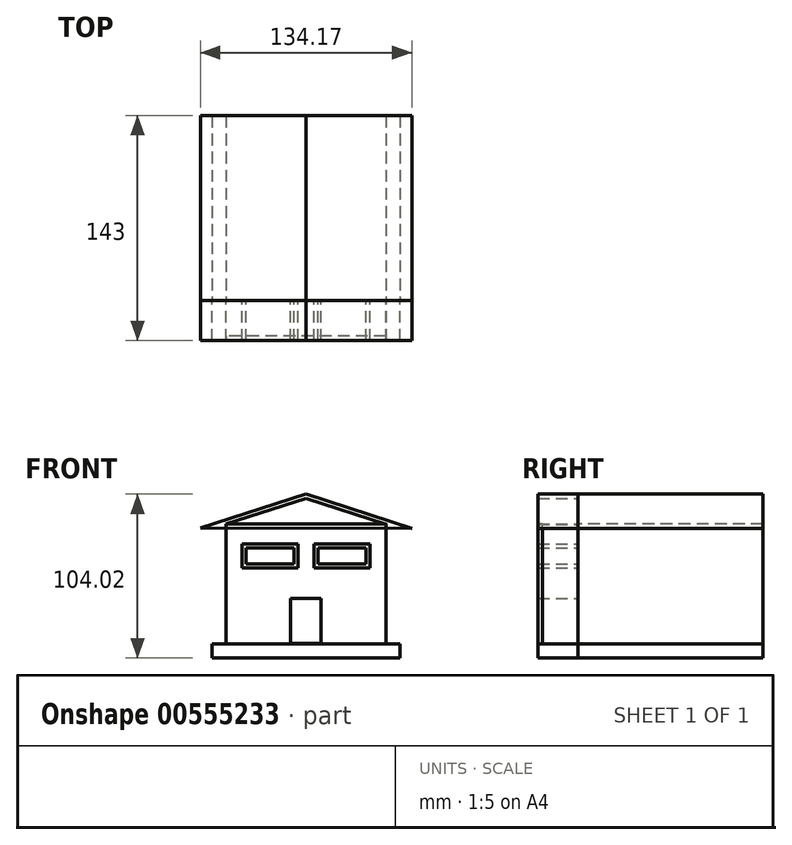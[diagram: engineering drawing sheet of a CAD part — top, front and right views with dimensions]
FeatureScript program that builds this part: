
annotation { "Feature Type Name" : "Feature", "Feature Type Description" : "" }
export const myFeature = defineFeature(function(context is Context, id is Id, definition is map)
    precondition{}
    {
        {
            var Q0;
            Q0=qCreatedBy(makeId("Front.planeOp"),FACE);
            var sketch = newSketch(context, id + "F0", { "sketchPlane" : qUnion([Q0])});
            skLineSegment(sketch, "E0.bottom", {"start": v(50.8, -38.1) * mm, "end": v(-50.8, -38.1) * mm});
            skLineSegment(sketch, "E0.top", {"start": v(50.8, 38.1) * mm, "end": v(-50.8, 38.1) * mm});
            skLineSegment(sketch, "E0.left", {"start": v(50.8, -38.1) * mm, "end": v(50.8, 38.1) * mm});
            skLineSegment(sketch, "E0.right", {"start": v(-50.8, -38.1) * mm, "end": v(-50.8, 38.1) * mm});
            skPoint(sketch, "E0.middle", {"position": v(0, 0) * mm});
            skSolve(sketch);
        }
        {
            var Q0;
            Q0=qCreatedBy(makeId("Front.planeOp"),FACE);
            var sketch = newSketch(context, id + "F1", { "sketchPlane" : qUnion([Q0])});
            skLineSegment(sketch, "E1.bottom", {"start": v(9.63, -37.6) * mm, "end": v(-9.63, -37.6) * mm});
            skLineSegment(sketch, "E1.top", {"start": v(9.63, -9.32) * mm, "end": v(-9.63, -9.32) * mm});
            skLineSegment(sketch, "E1.left", {"start": v(9.63, -37.6) * mm, "end": v(9.63, -9.32) * mm});
            skLineSegment(sketch, "E1.right", {"start": v(-9.63, -37.6) * mm, "end": v(-9.63, -9.32) * mm});
            skPoint(sketch, "E1.middle", {"position": v(0, -23.46) * mm});
            skSolve(sketch);
        }
        {
            var Q0;
            Q0=makeQuery(id+"F0.imprint","IMPRINT",FACE,{"disambiguationData":[TD([[makeQuery(id+"F0.imprint","IMPRINT",EDGE,{"derivedFrom":sQuery(id+"F0.wireOp",EDGE,"E0.bottom")}),-1.0]])]});
            var sketch = newSketch(context, id + "F2", { "sketchPlane" : qUnion([Q0])});
            skLineSegment(sketch, "E2.bottom", {"start": v(-41.8, -12.93) * mm, "end": v(-16.84, -12.93) * mm});
            skLineSegment(sketch, "E2.top", {"start": v(-41.8, -27.37) * mm, "end": v(-16.84, -27.37) * mm});
            skLineSegment(sketch, "E2.left", {"start": v(-41.8, -12.93) * mm, "end": v(-41.8, -27.37) * mm});
            skLineSegment(sketch, "E2.right", {"start": v(-16.84, -12.93) * mm, "end": v(-16.84, -27.37) * mm});
            skSolve(sketch);
        }
        {
            var Q0;
            Q0=makeQuery(id+"F0.imprint","IMPRINT",FACE,{"disambiguationData":[TD([[makeQuery(id+"F0.imprint","IMPRINT",EDGE,{"derivedFrom":sQuery(id+"F0.wireOp",EDGE,"E0.bottom")}),-1.0]])]});
            var sketch = newSketch(context, id + "F3", { "sketchPlane" : qUnion([Q0])});
            skLineSegment(sketch, "E3.0", {"start": v(-44.35, -10.4) * mm, "end": v(-14.3, -10.4) * mm});
            skLineSegment(sketch, "E3.1", {"start": v(-44.35, -10.4) * mm, "end": v(-44.35, -29.91) * mm});
            skLineSegment(sketch, "E3.2", {"start": v(-44.35, -29.91) * mm, "end": v(-14.3, -29.91) * mm});
            skLineSegment(sketch, "E3.3", {"start": v(-14.3, -10.4) * mm, "end": v(-14.3, -29.91) * mm});
            skSolve(sketch);
        }
        {
            var Q0;
            Q0=makeQuery(id+"F0.imprint","IMPRINT",FACE,{"disambiguationData":[TD([[makeQuery(id+"F0.imprint","IMPRINT",EDGE,{"derivedFrom":sQuery(id+"F0.wireOp",EDGE,"E0.bottom")}),-1.0]])]});
            var sketch = newSketch(context, id + "F4", { "sketchPlane" : qUnion([Q0])});
            skLineSegment(sketch, "E4.bottom", {"start": v(15.04, -13.54) * mm, "end": v(44.82, -13.54) * mm});
            skLineSegment(sketch, "E4.top", {"start": v(15.04, -28.88) * mm, "end": v(44.82, -28.88) * mm});
            skLineSegment(sketch, "E4.left", {"start": v(15.04, -13.54) * mm, "end": v(15.04, -28.88) * mm});
            skLineSegment(sketch, "E4.right", {"start": v(44.82, -13.54) * mm, "end": v(44.82, -28.88) * mm});
            skSolve(sketch);
        }
        {
            var Q0;
            Q0=makeQuery(id+"F0.imprint","IMPRINT",FACE,{"disambiguationData":[TD([[makeQuery(id+"F0.imprint","IMPRINT",EDGE,{"derivedFrom":sQuery(id+"F0.wireOp",EDGE,"E0.bottom")}),-1.0]])]});
            var sketch = newSketch(context, id + "F5", { "sketchPlane" : qUnion([Q0])});
            skLineSegment(sketch, "E5.0", {"start": v(12.5, -11) * mm, "end": v(47.36, -11) * mm});
            skLineSegment(sketch, "E5.1", {"start": v(12.5, -11) * mm, "end": v(12.5, -31.42) * mm});
            skLineSegment(sketch, "E5.2", {"start": v(12.5, -31.42) * mm, "end": v(47.36, -31.42) * mm});
            skLineSegment(sketch, "E5.3", {"start": v(47.36, -11) * mm, "end": v(47.36, -31.42) * mm});
            skSolve(sketch);
        }
        {
            var Q0;
            Q0=qCreatedBy(makeId("Front.planeOp"),FACE);
            var sketch = newSketch(context, id + "F6", { "sketchPlane" : qUnion([Q0])});
            skLineSegment(sketch, "E6.bottom", {"start": v(-38.1, 22.86) * mm, "end": v(-7.62, 22.86) * mm});
            skLineSegment(sketch, "E6.top", {"start": v(-38.1, 12.7) * mm, "end": v(-7.62, 12.7) * mm});
            skLineSegment(sketch, "E6.left", {"start": v(-38.1, 22.86) * mm, "end": v(-38.1, 12.7) * mm});
            skLineSegment(sketch, "E6.right", {"start": v(-7.62, 22.86) * mm, "end": v(-7.62, 12.7) * mm});
            skLineSegment(sketch, "E7.bottom", {"start": v(7.62, 22.86) * mm, "end": v(38.1, 22.86) * mm});
            skLineSegment(sketch, "E7.top", {"start": v(7.62, 12.7) * mm, "end": v(38.1, 12.7) * mm});
            skLineSegment(sketch, "E7.left", {"start": v(7.62, 22.86) * mm, "end": v(7.62, 12.7) * mm});
            skLineSegment(sketch, "E7.right", {"start": v(38.1, 22.86) * mm, "end": v(38.1, 12.7) * mm});
            skSolve(sketch);
        }
        {
            var Q0;
            Q0=qCreatedBy(makeId("Front.planeOp"),FACE);
            var sketch = newSketch(context, id + "F7", { "sketchPlane" : qUnion([Q0])});
            skLineSegment(sketch, "E8.0", {"start": v(-40.64, 25.4) * mm, "end": v(-5.08, 25.4) * mm});
            skLineSegment(sketch, "E8.1", {"start": v(-40.64, 25.4) * mm, "end": v(-40.64, 10.16) * mm});
            skLineSegment(sketch, "E8.2", {"start": v(-40.64, 10.16) * mm, "end": v(-5.08, 10.16) * mm});
            skLineSegment(sketch, "E8.3", {"start": v(-5.08, 25.4) * mm, "end": v(-5.08, 10.16) * mm});
            skLineSegment(sketch, "E9.0", {"start": v(40.64, 25.4) * mm, "end": v(40.64, 10.16) * mm});
            skLineSegment(sketch, "E9.1", {"start": v(5.08, 25.4) * mm, "end": v(40.64, 25.4) * mm});
            skLineSegment(sketch, "E9.2", {"start": v(5.08, 25.4) * mm, "end": v(5.08, 10.16) * mm});
            skLineSegment(sketch, "E9.3", {"start": v(5.08, 10.16) * mm, "end": v(40.64, 10.16) * mm});
            skSolve(sketch);
        }
        {
            var Q0;
            Q0=qCreatedBy(makeId("Front.planeOp"),FACE);
            var sketch = newSketch(context, id + "F8", { "sketchPlane" : qUnion([Q0])});
            skLineSegment(sketch, "E10", {"start": v(-50.8, 38.1) * mm, "end": v(0, 54.36) * mm});
            skLineSegment(sketch, "E11", {"start": v(0, 54.36) * mm, "end": v(51.1, 37.73) * mm});
            skLineSegment(sketch, "E12", {"start": v(51.1, 37.73) * mm, "end": v(-50.8, 38.1) * mm});
            skSolve(sketch);
        }
        {
            var Q0;
            Q0=qCreatedBy(makeId("Front.planeOp"),FACE);
            var sketch = newSketch(context, id + "F9", { "sketchPlane" : qUnion([Q0])});
            skLineSegment(sketch, "E13.0", {"start": v(-66.88, 35.62) * mm, "end": v(0, 57.03) * mm});
            skLineSegment(sketch, "E13.1", {"start": v(67.29, 35.13) * mm, "end": v(-66.88, 35.62) * mm});
            skLineSegment(sketch, "E13.2", {"start": v(0, 57.03) * mm, "end": v(67.29, 35.13) * mm});
            skSolve(sketch);
        }
        {
            var Q0;
            Q0=qCreatedBy(makeId("Front.planeOp"),FACE);
            var sketch = newSketch(context, id + "F10", { "sketchPlane" : qUnion([Q0])});
            skLineSegment(sketch, "E14.bottom", {"start": v(-59.7, -38.1) * mm, "end": v(59.7, -38.1) * mm});
            skLineSegment(sketch, "E14.top", {"start": v(-59.7, -46.99) * mm, "end": v(59.7, -46.99) * mm});
            skLineSegment(sketch, "E14.left", {"start": v(-59.7, -38.1) * mm, "end": v(-59.7, -46.99) * mm});
            skLineSegment(sketch, "E14.right", {"start": v(59.7, -38.1) * mm, "end": v(59.7, -46.99) * mm});
            skSolve(sketch);
        }
        {
            var Q0;
            Q0=makeQuery(id+"F8.imprint","IMPRINT",FACE,{"disambiguationData":[TD([[makeQuery(id+"F8.imprint","IMPRINT",EDGE,{"derivedFrom":sQuery(id+"F8.wireOp",EDGE,"E10")}),-1.0]])]});
            var Q1;
            Q1=makeQuery(id+"F6.imprint","IMPRINT",FACE,{"disambiguationData":[TD([[makeQuery(id+"F6.imprint","IMPRINT",EDGE,{"derivedFrom":sQuery(id+"F6.wireOp",EDGE,"E6.bottom")}),-1.0]])]});
            var Q2;
            Q2=makeQuery(id+"F2.imprint","IMPRINT",FACE,{"disambiguationData":[TD([[makeQuery(id+"F2.imprint","IMPRINT",EDGE,{"derivedFrom":sQuery(id+"F2.wireOp",EDGE,"E2.bottom")}),-1.0]])]});
            var Q3;
            Q3=makeQuery(id+"F2.imprint","IMPRINT",FACE,{"disambiguationData":[TD([[makeQuery(id+"F2.imprint","IMPRINT",EDGE,{"derivedFrom":sQuery(id+"F2.wireOp",EDGE,"E2.bottom")}),1.0]])]});
            var Q4;
            Q4=makeQuery(id+"F6.imprint","IMPRINT",FACE,{"disambiguationData":[TD([[makeQuery(id+"F6.imprint","IMPRINT",EDGE,{"derivedFrom":sQuery(id+"F6.wireOp",EDGE,"E7.bottom")}),-1.0]])]});
            var Q5;
            Q5=makeQuery(id+"F3.imprint","IMPRINT",FACE,{"disambiguationData":[TD([[makeQuery(id+"F3.imprint","IMPRINT",EDGE,{"derivedFrom":sQuery(id+"F3.wireOp",EDGE,"E3.0")}),-1.0]])]});
            var Q6;
            Q6=makeQuery(id+"F3.imprint","IMPRINT",FACE,{"disambiguationData":[TD([[makeQuery(id+"F3.imprint","IMPRINT",EDGE,{"derivedFrom":sQuery(id+"F3.wireOp",EDGE,"E3.0")}),1.0]])]});
            var Q7;
            Q7=makeQuery(id+"F0.imprint","IMPRINT",FACE,{"disambiguationData":[TD([[makeQuery(id+"F0.imprint","IMPRINT",EDGE,{"derivedFrom":sQuery(id+"F0.wireOp",EDGE,"E0.bottom")}),-1.0]])]});
            var Q8;
            Q8=makeQuery(id+"F4.imprint","IMPRINT",FACE,{"disambiguationData":[TD([[makeQuery(id+"F4.imprint","IMPRINT",EDGE,{"derivedFrom":sQuery(id+"F4.wireOp",EDGE,"E4.bottom")}),-1.0]])]});
            var Q9;
            Q9=makeQuery(id+"F4.imprint","IMPRINT",FACE,{"disambiguationData":[TD([[makeQuery(id+"F4.imprint","IMPRINT",EDGE,{"derivedFrom":sQuery(id+"F4.wireOp",EDGE,"E4.bottom")}),1.0]])]});
            var Q10;
            Q10=makeQuery(id+"F9.imprint","IMPRINT",FACE,{"disambiguationData":[TD([[makeQuery(id+"F9.imprint","IMPRINT",EDGE,{"derivedFrom":sQuery(id+"F9.wireOp",EDGE,"E13.0")}),-1.0]])]});
            var Q11;
            Q11=makeQuery(id+"F5.imprint","IMPRINT",FACE,{"disambiguationData":[TD([[makeQuery(id+"F5.imprint","IMPRINT",EDGE,{"derivedFrom":sQuery(id+"F5.wireOp",EDGE,"E5.0")}),-1.0]])]});
            var Q12;
            Q12=makeQuery(id+"F5.imprint","IMPRINT",FACE,{"disambiguationData":[TD([[makeQuery(id+"F5.imprint","IMPRINT",EDGE,{"derivedFrom":sQuery(id+"F5.wireOp",EDGE,"E5.0")}),1.0]])]});
            var Q13;
            Q13=makeQuery(id+"F1.imprint","IMPRINT",FACE,{"disambiguationData":[TD([[makeQuery(id+"F1.imprint","IMPRINT",EDGE,{"derivedFrom":sQuery(id+"F1.wireOp",EDGE,"E1.bottom")}),-1.0]])]});
            var Q14;
            Q14=makeQuery(id+"F7.imprint","IMPRINT",FACE,{"disambiguationData":[TD([[makeQuery(id+"F7.imprint","IMPRINT",EDGE,{"derivedFrom":sQuery(id+"F7.wireOp",EDGE,"E8.0")}),-1.0]])]});
            var Q15;
            Q15=makeQuery(id+"F7.imprint","IMPRINT",FACE,{"disambiguationData":[TD([[makeQuery(id+"F7.imprint","IMPRINT",EDGE,{"derivedFrom":sQuery(id+"F7.wireOp",EDGE,"E9.0")}),-1.0]])]});
            var Q16;
            Q16=makeQuery(id+"F10.imprint","IMPRINT",FACE,{"disambiguationData":[TD([[makeQuery(id+"F10.imprint","IMPRINT",EDGE,{"derivedFrom":sQuery(id+"F10.wireOp",EDGE,"E14.bottom")}),-1.0]])]});
            extrude(context, id + "F11", {"entities" : qUnion([Q0, Q1, Q2, Q3, Q4, Q5, Q6, Q7, Q8, Q9, Q10, Q11, Q12, Q13, Q14, Q15, Q16]), "depth" : 25.4 * mm, "offsetDistance" : 25.4 * mm});
        }
        {
            var Q0;
            Q0=makeQuery(id+"F11.opExtrude","CAP_FACE",FACE,{"disambiguationData":[OSD([sQuery(id+"F10.wireOp",EDGE,"E14.bottom"),sQuery(id+"F10.wireOp",EDGE,"E14.top"),sQuery(id+"F10.wireOp",EDGE,"E14.left"),sQuery(id+"F10.wireOp",EDGE,"E14.right")])],"isStart":true});
            var Q1;
            {var subQ0=sQuery(id+"F0.wireOp",EDGE,"E0.right");var subQ1=sQuery(id+"F0.wireOp",EDGE,"E0.left");var subQ2=sQuery(id+"F0.wireOp",EDGE,"E0.top");var subQ3=sQuery(id+"F0.wireOp",EDGE,"E0.bottom");Q1=makeQuery(id+"F11.opExtrude","CAP_FACE",FACE,{"disambiguationData":[OSD([subQ3,subQ2,subQ1,subQ0]),TDD([makeQuery(id+"F0.imprint","IMPRINT",EDGE,{"derivedFrom":subQ3}),makeQuery(id+"F0.imprint","IMPRINT",EDGE,{"derivedFrom":subQ2}),makeQuery(id+"F0.imprint","IMPRINT",EDGE,{"derivedFrom":subQ1}),makeQuery(id+"F0.imprint","IMPRINT",EDGE,{"derivedFrom":subQ0})])],"isStart":true});}
            var Q2;
            Q2=makeQuery(id+"F11.opExtrude","CAP_FACE",FACE,{"disambiguationData":[OSD([sQuery(id+"F9.wireOp",EDGE,"E13.0"),sQuery(id+"F9.wireOp",EDGE,"E13.1"),sQuery(id+"F9.wireOp",EDGE,"E13.2")])],"isStart":true});
            extrude(context, id + "F12", {"entities" : qUnion([Q0, Q1, Q2]), "depth" : 117.6 * mm, "offsetDistance" : 25.4 * mm});
        }
        {
            var Q0;
            {var subQ0=sQuery(id+"F0.wireOp",EDGE,"E0.right");var subQ1=sQuery(id+"F0.wireOp",EDGE,"E0.left");var subQ2=sQuery(id+"F0.wireOp",EDGE,"E0.top");var subQ3=sQuery(id+"F0.wireOp",EDGE,"E0.bottom");Q0=makeQuery(id+"F11.opExtrude","CAP_FACE",FACE,{"disambiguationData":[OSD([subQ3,subQ2,subQ1,subQ0]),TDD([makeQuery(id+"F0.imprint","IMPRINT",EDGE,{"derivedFrom":subQ3}),makeQuery(id+"F0.imprint","IMPRINT",EDGE,{"derivedFrom":subQ2}),makeQuery(id+"F0.imprint","IMPRINT",EDGE,{"derivedFrom":subQ1}),makeQuery(id+"F0.imprint","IMPRINT",EDGE,{"derivedFrom":subQ0})])],"isStart":false});}
            extrude(context, id + "F13", {"entities" : qUnion([Q0]), "oppositeDirection" : true, "depth" : 3.05 * mm, "offsetDistance" : 25.4 * mm});
        }
    });
